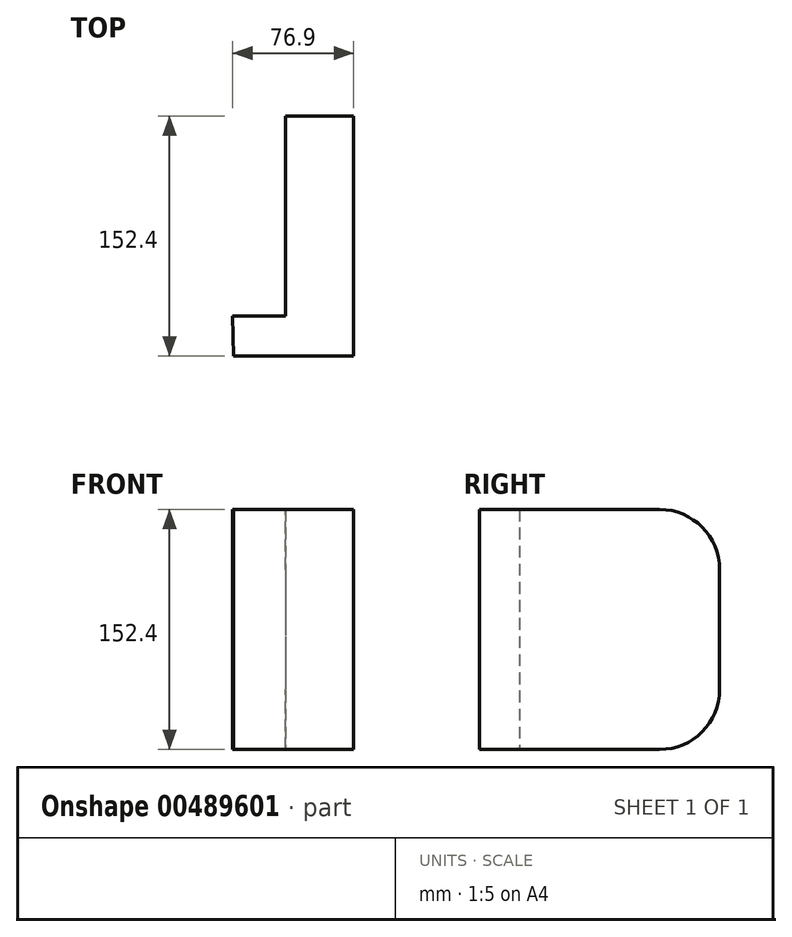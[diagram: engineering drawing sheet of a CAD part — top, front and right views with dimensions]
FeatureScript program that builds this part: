
annotation { "Feature Type Name" : "Feature", "Feature Type Description" : "" }
export const myFeature = defineFeature(function(context is Context, id is Id, definition is map)
    precondition{}
    {
        {
            var Q0;
            Q0=qCreatedBy(makeId("Top.planeOp"),FACE);
            var sketch = newSketch(context, id + "F0", { "sketchPlane" : qUnion([Q0])});
            skLineSegment(sketch, "E0.bottom", {"start": v(-21.64, 76.2) * mm, "end": v(21.64, 76.2) * mm});
            skLineSegment(sketch, "E0.top", {"start": v(-21.64, -76.2) * mm, "end": v(21.64, -76.2) * mm});
            skLineSegment(sketch, "E0.left", {"start": v(-21.64, 76.2) * mm, "end": v(-21.64, -50.8) * mm});
            skLineSegment(sketch, "E0.right", {"start": v(21.64, 76.2) * mm, "end": v(21.64, -76.2) * mm});
            skPoint(sketch, "E0.middle", {"position": v(0, 0) * mm});
            skLineSegment(sketch, "E1", {"start": v(-21.64, -76.2) * mm, "end": v(-54.56, -76.2) * mm});
            skLineSegment(sketch, "E2", {"start": v(-21.64, -50.8) * mm, "end": v(-55.26, -50.8) * mm});
            skLineSegment(sketch, "E3", {"start": v(-55.26, -50.8) * mm, "end": v(-54.56, -76.2) * mm});
            skSolve(sketch);
        }
        {
            var Q0;
            Q0 = qSketchRegion(id + "F0", true);
            extrude(context, id + "F1", {"entities" : qUnion([Q0]), "endBound" : BoundingType.SYMMETRIC, "depth" : 152.4 * mm});
        }
        {
            var Q0;
            Q0=makeQuery(id+"F1.opExtrude","CAP_EDGE",EDGE,{"disambiguationData":[OSD([sQuery(id+"F0.wireOp",EDGE,"E0.bottom")])],"isStart":true});
            var Q1;
            Q1=makeQuery(id+"F1.opExtrude","CAP_EDGE",EDGE,{"disambiguationData":[OSD([sQuery(id+"F0.wireOp",EDGE,"E0.bottom")])],"isStart":false});
            fillet(context, id + "F2", {"entities" : qUnion([Q0, Q1]), "radius" : 38.1 * mm, "tangentPropagation" : true, "allowEdgeOverflow" : false});
        }
    });
